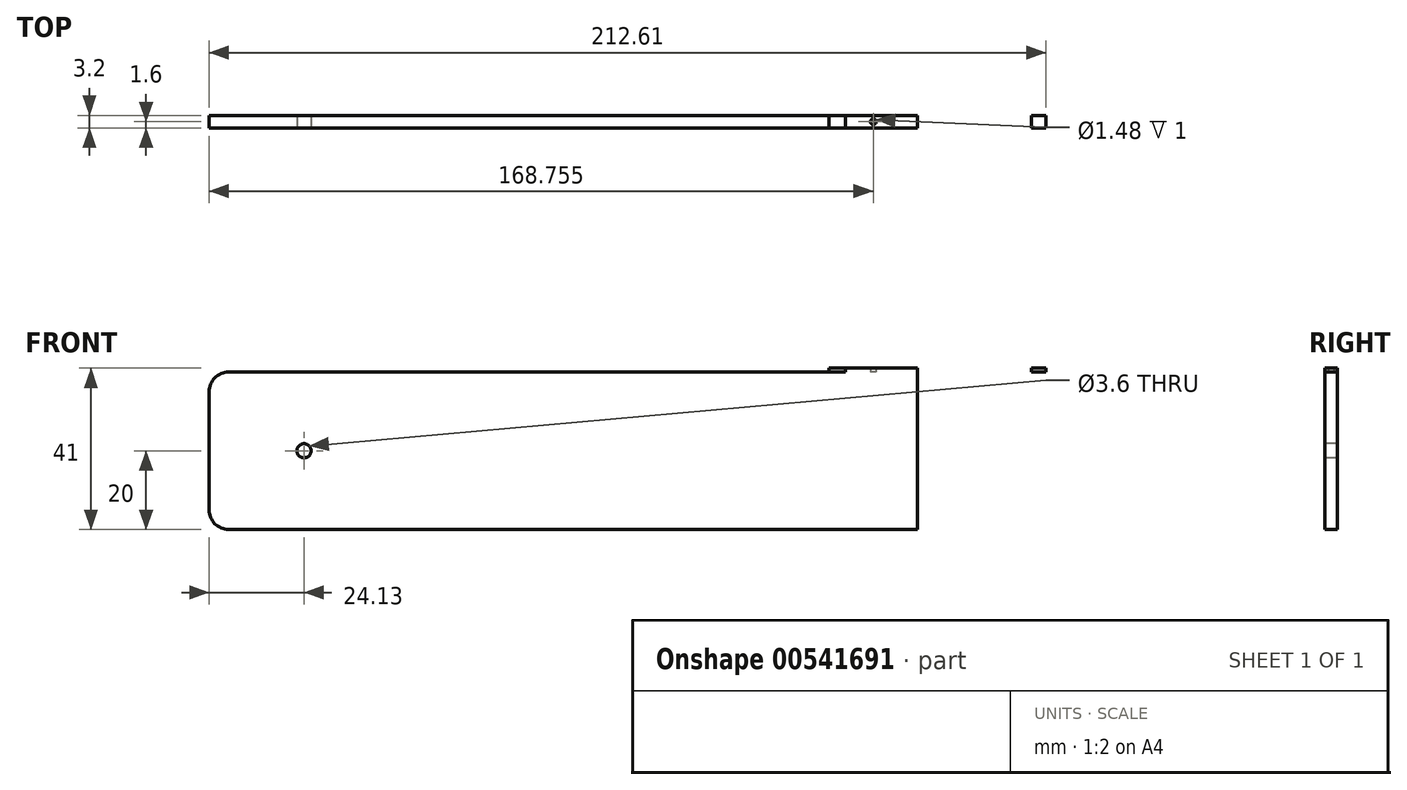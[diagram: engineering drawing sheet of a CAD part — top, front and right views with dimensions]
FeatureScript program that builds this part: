
annotation { "Feature Type Name" : "Feature", "Feature Type Description" : "" }
export const myFeature = defineFeature(function(context is Context, id is Id, definition is map)
    precondition{}
    {
        {
            var Q0;
            Q0=qCreatedBy(makeId("Front.planeOp"),FACE);
            var sketch = newSketch(context, id + "F0", { "sketchPlane" : qUnion([Q0])});
            skLineSegment(sketch, "E0.bottom", {"start": v(90, 20) * mm, "end": v(-90, 20) * mm});
            skLineSegment(sketch, "E0.top", {"start": v(90, -20) * mm, "end": v(-90, -20) * mm});
            skLineSegment(sketch, "E0.left", {"start": v(90, 20) * mm, "end": v(90, -20) * mm});
            skLineSegment(sketch, "E0.right", {"start": v(-90, 20) * mm, "end": v(-90, -20) * mm});
            skPoint(sketch, "E0.middle", {"position": v(0, 0) * mm});
            skSolve(sketch);
        }
        {
            var Q0;
            Q0 = qSketchRegion(id + "F0", true);
            extrude(context, id + "F1", {"entities" : qUnion([Q0]), "endBound" : BoundingType.SYMMETRIC, "depth" : 3.2 * mm, "offsetDistance" : 25 * mm});
        }
        {
            var Q0;
            Q0=makeQuery(id+"F1.opExtrude","SWEPT_EDGE",EDGE,{"disambiguationData":[OSD([sQuery(id+"F0.wireOp",EDGE,"E0.bottom"),sQuery(id+"F0.wireOp",EDGE,"E0.right")])]});
            var Q1;
            Q1=makeQuery(id+"F1.opExtrude","SWEPT_EDGE",EDGE,{"disambiguationData":[OSD([sQuery(id+"F0.wireOp",EDGE,"E0.top"),sQuery(id+"F0.wireOp",EDGE,"E0.right")])]});
            fillet(context, id + "F2", {"entities" : qUnion([Q0, Q1]), "radius" : 5 * mm, "tangentPropagation" : true, "allowEdgeOverflow" : false});
        }
        {
            var Q0;
            Q0=makeQuery(id+"F1.opExtrude","CAP_FACE",FACE,{"disambiguationData":[OSD([sQuery(id+"F0.wireOp",EDGE,"E0.bottom"),sQuery(id+"F0.wireOp",EDGE,"E0.top"),sQuery(id+"F0.wireOp",EDGE,"E0.left"),sQuery(id+"F0.wireOp",EDGE,"E0.right")])],"isStart":false});
            var sketch = newSketch(context, id + "F3", { "sketchPlane" : qUnion([Q0])});
            skCircle(sketch, "E1", {"center": v(-65.87, 0) * mm, "radius": 1.8 * mm});
            skPoint(sketch, "E1.centerSnap0", {"position": v(-90, 0) * mm});
            skSolve(sketch);
        }
        {
            var Q0;
            Q0 = qSketchRegion(id + "F3", true);
            extrude(context, id + "F4", {"entities" : qUnion([Q0]), "operationType" : NewBodyOperationType.REMOVE, "oppositeDirection" : true, "depth" : 4.1 * mm, "offsetDistance" : 25 * mm});
        }
        {
            var Q0;
            Q0=makeQuery(id+"F1.opExtrude","SWEPT_FACE",FACE,{"disambiguationData":[OSD([sQuery(id+"F0.wireOp",EDGE,"E0.bottom"),sQuery(id+"F0.wireOp",EDGE,"GM8NByEf-oLmy-gmvQ-ajo0-c5iNKBjy0ZZF")])]});
            var sketch = newSketch(context, id + "F5", { "sketchPlane" : qUnion([Q0])});
            skLineSegment(sketch, "E2.bottom", {"start": v(118.94, -1.6) * mm, "end": v(122.6, -1.6) * mm});
            skLineSegment(sketch, "E2.top", {"start": v(118.94, 1.6) * mm, "end": v(122.6, 1.6) * mm});
            skLineSegment(sketch, "E2.left", {"start": v(118.94, -1.6) * mm, "end": v(118.94, 1.6) * mm});
            skLineSegment(sketch, "E2.right", {"start": v(122.6, -1.6) * mm, "end": v(122.6, 1.6) * mm});
            skPoint(sketch, "E2.middle", {"position": v(120.77, 0) * mm});
            skSolve(sketch);
        }
        {
            var Q0;
            Q0 = qSketchRegion(id + "F5", true);
            extrude(context, id + "F6", {"entities" : qUnion([Q0]), "operationType" : NewBodyOperationType.ADD, "depth" : 1 * mm, "offsetDistance" : 25 * mm});
        }
        {
            var Q0;
            Q0=makeQuery(id+"F1.opExtrude","SWEPT_FACE",FACE,{"disambiguationData":[OSD([sQuery(id+"F0.wireOp",EDGE,"E0.bottom")])]});
            var sketch = newSketch(context, id + "F7", { "sketchPlane" : qUnion([Q0])});
            skLineSegment(sketch, "E3.bottom", {"start": v(90, 1.6) * mm, "end": v(85.8, 1.6) * mm});
            skLineSegment(sketch, "E3.top", {"start": v(90, -1.6) * mm, "end": v(85.8, -1.6) * mm});
            skLineSegment(sketch, "E3.left", {"start": v(90, 1.6) * mm, "end": v(90, -1.6) * mm});
            skLineSegment(sketch, "E3.right", {"start": v(85.8, 1.6) * mm, "end": v(85.8, -1.6) * mm});
            skPoint(sketch, "E3.middle", {"position": v(87.9, 0) * mm});
            skSolve(sketch);
        }
        {
            var Q0;
            Q0 = qSketchRegion(id + "F7", true);
            extrude(context, id + "F8", {"entities" : qUnion([Q0]), "operationType" : NewBodyOperationType.ADD, "depth" : 1 * mm, "offsetDistance" : 25 * mm});
        }
        {
            var Q0;
            Q0=makeQuery(id+"F1.opExtrude","SWEPT_FACE",FACE,{"disambiguationData":[OSD([sQuery(id+"F0.wireOp",EDGE,"E0.bottom")])]});
            var sketch = newSketch(context, id + "F9", { "sketchPlane" : qUnion([Q0])});
            skLineSegment(sketch, "E4.bottom", {"start": v(85.8, 1.6) * mm, "end": v(71.71, 1.6) * mm});
            skLineSegment(sketch, "E4.top", {"start": v(85.8, -1.6) * mm, "end": v(71.71, -1.6) * mm});
            skLineSegment(sketch, "E4.left", {"start": v(85.8, 1.6) * mm, "end": v(85.8, -1.6) * mm});
            skLineSegment(sketch, "E4.right", {"start": v(71.71, 1.6) * mm, "end": v(71.71, -1.6) * mm});
            skPoint(sketch, "E4.middle", {"position": v(78.76, 0) * mm});
            skLineSegment(sketch, "E5", {"start": v(77.12, 1.6) * mm, "end": v(77.12, -1.6) * mm});
            skLineSegment(sketch, "E6", {"start": v(79.98, 1.6) * mm, "end": v(79.98, -1.6) * mm});
            skCircle(sketch, "E7", {"center": v(78.76, 0) * mm, "radius": 0.74 * mm});
            skSolve(sketch);
        }
        {
            var Q0;
            {var subQ0=sQuery(id+"F9.wireOp",EDGE,"E4.right");Q0=makeQuery(id+"F9.imprint","IMPRINT",FACE,{"disambiguationData":[TD([[makeQuery(id+"F9.imprint","IMPRINT",EDGE,{"derivedFrom":subQ0}),-1.0]])]});}
            var sketch = newSketch(context, id + "F10", { "sketchPlane" : qUnion([Q0])});
            skLineSegment(sketch, "E8.bottom", {"start": v(71.7, 1.55) * mm, "end": v(67.52, 1.55) * mm});
            skLineSegment(sketch, "E8.top", {"start": v(71.7, -1.55) * mm, "end": v(67.52, -1.55) * mm});
            skLineSegment(sketch, "E8.left", {"start": v(71.7, 1.55) * mm, "end": v(71.7, -1.55) * mm});
            skLineSegment(sketch, "E8.right", {"start": v(67.52, 1.55) * mm, "end": v(67.52, -1.55) * mm});
            skPoint(sketch, "E8.middle", {"position": v(69.6, 0) * mm});
            skSolve(sketch);
        }
        {
            var Q0;
            Q0 = qSketchRegion(id + "F10", true);
            extrude(context, id + "F11", {"entities" : qUnion([Q0]), "operationType" : NewBodyOperationType.ADD, "depth" : 1 * mm, "offsetDistance" : 25 * mm});
        }
        {
            var Q0;
            Q0 = qSketchRegion(id + "F9", true);
            extrude(context, id + "F12", {"entities" : qUnion([Q0]), "operationType" : NewBodyOperationType.ADD, "depth" : 1 * mm, "offsetDistance" : 25 * mm});
        }
    });
